# Revit family: Shower-Showerhead-KOHLER-Moxie-K-9245
name_source: partatom
category: Plumbing Fixtures
revit_build: Autodesk Revit 2015 (Build: 20140606_1530(x64)
units: mm (PartAtom-declared; Revit-internal decimal feet)

## types (9) — shared parameters
ADA Compliant = No
Assembly Code = D2010700
CW Connection = No
Cold Water Inlet = Cold Water Inlet
Date Modified = 02/18/2019
Default Elevation = 0"
Drain Included = No
HW Connection = Yes
Height = 4 3/16"
Hot Water Inlet = Hot Water Inlet
Length = 5"
Manufacturer = KOHLER Co.
MasterFormat 1995 = 15410
MasterFormat 2004 = 22.41.23
Material = Premium Metal Construction
Panel Thickness = 0"
Pressure = 45.00 psi
Product Documentation Link = https://www.us.kohler.com
Product Name = Moxie
Product Page URL = http://www.us.kohler.com
Tempered Water Inlet = Tempered Water Inlet
URL = https://www.us.kohler.com
Vent Connection = No
Waste Connection = No
Waste Water Outlet = Waste Water Outlet
Width = 5"

## per-type parameters (varying)
| type | Description | Finish | Flow Rate | Model | Type | WaterSense Certified |
| 2.0 GPM,2BZ-Oil-Rubbed Bronze | 2.0 gpm single-function showerhead with wireless speaker | Kohler-Metal-2BZ-Oil_Rubbed_Bronze | 2 GPM | K-9245-E-2BZ | 11 | Yes |
| 2.0 GPM,BN-Vibrant Brushed Nickel | 2.0 gpm single-function showerhead with wireless speaker | Kohler-Metal-BN-Vibrant_Brushed_Nickel | 2 GPM | K-9245-E-BN | 10 | Yes |
| 2.5 GPM,2BZ-Oil-Rubbed Bronze | 2.5 gpm single-function showerhead with wireless speaker | Kohler-Metal-2BZ-Oil_Rubbed_Bronze | 3 GPM | K-9245-2BZ | 7 | No |
| 2.5 GPM,BN-Vibrant Brushed Nickel | 2.5 gpm single-function showerhead with wireless speaker | Kohler-Metal-BN-Vibrant_Brushed_Nickel | 3 GPM | K-9245-BN | 6 | No |
| 2.5 GPM,CP-Polished Chrome | 2.5 gpm single-function showerhead with wireless speaker | Kohler-Metal-CP-Polished_Chrome | 3 GPM | K-9245-CP | 5 | No |
| 1.75 GPM,0-White | 1.75 gpm single-function showerhead with wireless speaker | Kohler-Metal-0-White | 2 GPM | K-9245-G-0 | 4 | Yes |
| 1.75 GPM,2BZ-Oil-Rubbed Bronze | 1.75 gpm single-function showerhead with wireless speaker | Kohler-Metal-2BZ-Oil_Rubbed_Bronze | 2 GPM | K-9245-G-2BZ | 3 | Yes |
| 1.75 GPM,BN-Vibrant Brushed Nickel | 1.75 gpm single-function showerhead with wireless speaker | Kohler-Metal-BN-Vibrant_Brushed_Nickel | 2 GPM | K-9245-G-BN | 2 | Yes |
| 1.75 GPM,CP-Polished Chrome | 1.75 gpm single-function showerhead with wireless speaker | Kohler-Metal-CP-Polished_Chrome | 2 GPM | K-9245-G-CP | 1 | Yes |

## geometry (parser evidence)
native form markers: Sweep x3
no freeform markers — native parametric forms only
